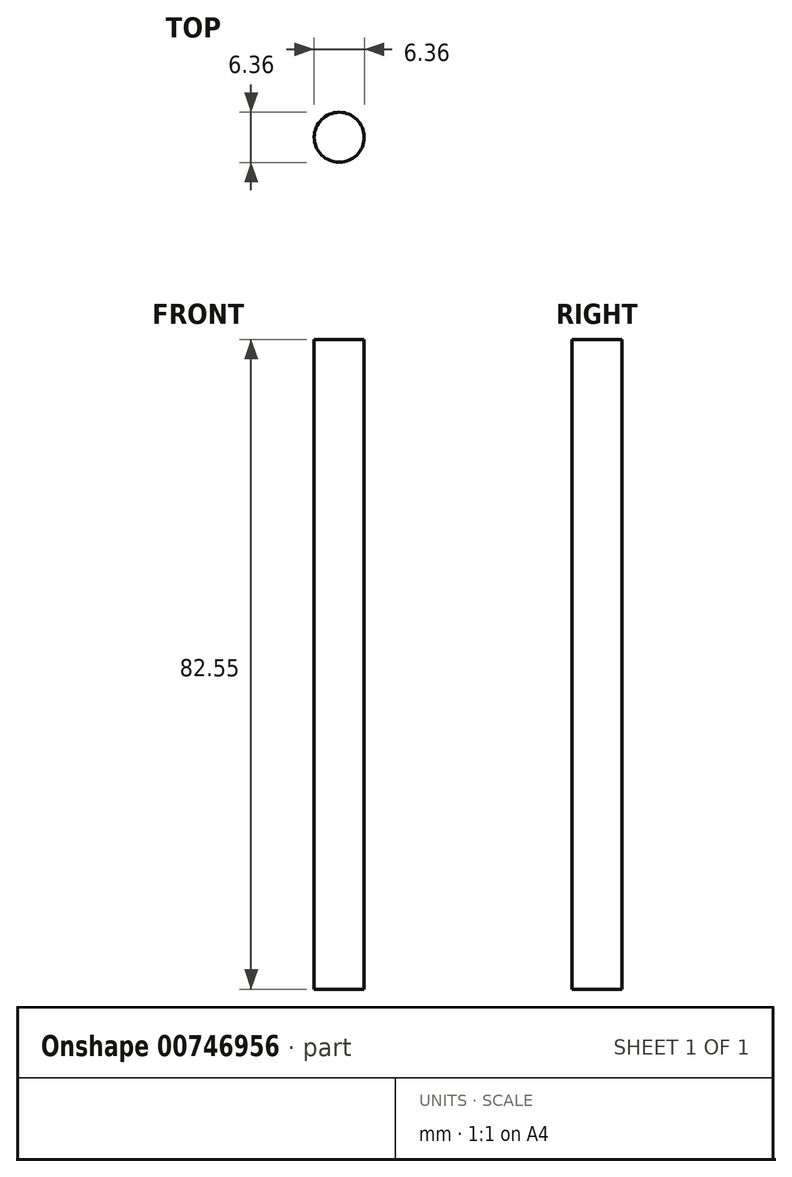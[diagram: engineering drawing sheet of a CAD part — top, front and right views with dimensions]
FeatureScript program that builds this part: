
annotation { "Feature Type Name" : "Feature", "Feature Type Description" : "" }
export const myFeature = defineFeature(function(context is Context, id is Id, definition is map)
    precondition{}
    {
        {
            var Q0;
            Q0=qCreatedBy(makeId("Top.planeOp"),FACE);
            var sketch = newSketch(context, id + "F0", { "sketchPlane" : qUnion([Q0])});
            skCircle(sketch, "E0", {"center": v(0, 0) * mm, "radius": 3.18 * mm});
            skSolve(sketch);
        }
        {
            var Q0;
            Q0=makeQuery(id+"F0.imprint","IMPRINT",FACE,{"disambiguationData":[TD([[makeQuery(id+"F0.imprint","IMPRINT",EDGE,{"derivedFrom":sQuery(id+"F0.wireOp",EDGE,"E0")}),1.0]])]});
            extrude(context, id + "F1", {"entities" : qUnion([Q0]), "depth" : 82.55 * mm, "offsetDistance" : 25.4 * mm});
        }
    });
